# Revit family: Control_Panels-Lutron-QS_Smart_Power_Panel
name_source: partatom
category: Electrical Equipment
revit_build: Autodesk Revit 2017 (Build: 20160720_1515(x64)
units: mm (PartAtom-declared; Revit-internal decimal feet)

## family parameters
Cut with Voids When Loaded = No
Host = Face
OmniClass Number = 23.80.30.11.17
OmniClass Title = Distribution Boards and Control Panels
Panel Configuration = Two Columns, Circuits Across
Part Type = Panelboard
Room Calculation Point = No
Round Connector Dimension = Use Radius
Shared = No

## types (2) — shared parameters
59 Panel Size = Yes
Assembly Code = D5020
Description = 30-Output Configurable Smart Enclosure
Electrical Connector Distance = 59 "
Finish = Steel - Lutron - Black
Frequency = 60 Hz
Ground Bus = Yes
Instruction Sheet Link = http://www.lutron.com
Load Classification = Power
MCB Rating = 1 A
Manufacturer = Lutron Electronics Co., Inc
Manufacturer Fax Number = 610-282-1243
Model = QSPS-30PNL-NPM
Neutral Bus = Yes
Neutral Rating = 0.00%
Number of Poles = 1
Overall Depth = 4.28 "
Overall Height = 59.5 "
Overall Width = 15.875 "
Performance URL = http://www.lutron.com
Phase = 1
Power Factor = 1
Product Documentation Link = http://www.lutron.com
Product Name = 30-Output Configurable Smart Enclosure
Product Page URL = http://www.lutron.com
Series = Sivoia QS
SubFeed Lugs = No
URL = http://www.lutron.com
Unit Weight = 0.00 lb
Version = 2017 - v1.0a
Video Link = https://www.youtube.com
Warranty URL = http://www.lutron.com
zero-valued in all types: Cost, Default Elevation

## per-type parameters (varying)
| type | Electrical Potential | Feed Through Control Circuit Voltage | Voltage |
| QSPS-30PNL-NPM - 120V | 120 V | 120 V | 120.00 V |
| QSPS-30PNL-NPM - 240V | 240 V | 240 V | 240.00 V |

## geometry (parser evidence)
native form markers: Sweep x2
no freeform markers — native parametric forms only
